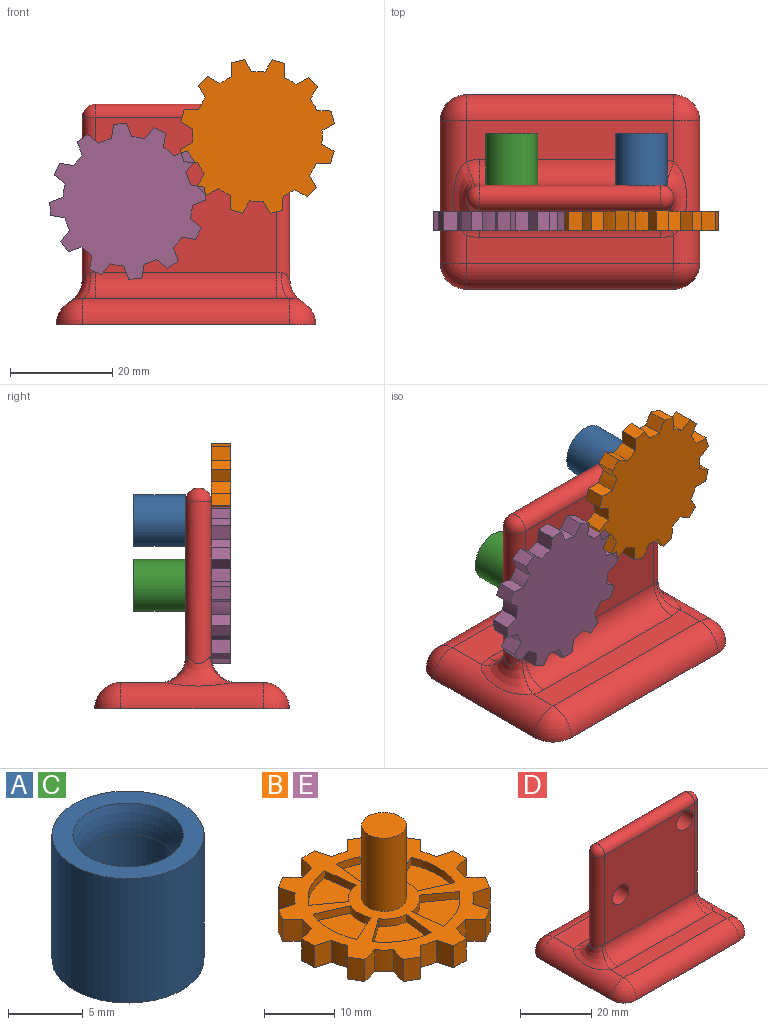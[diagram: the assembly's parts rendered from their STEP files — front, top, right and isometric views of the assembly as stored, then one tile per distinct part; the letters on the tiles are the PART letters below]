
ASSEMBLY  parts=5 mates=4
PART A: 6 faces, bbox 10.2x10.2x11.6 mm
  f0: cylinder r=3.17mm len=6.35mm, axis (0,0,-1), area 107.8mm2, adj f3,f4
  f1: cylinder r=5.08mm len=10.16mm, axis (0,0,-1), area 324.3mm2, adj f2,f5
  f2: plane 10.16x10.16mm, normal (0,0,1), area 38.5mm2, adj f1,f3
  f3: torus R=8.26mm, axis (0,0,1), area 48.2mm2, adj f0,f2
  f4: plane 6.35x6.35mm, normal (0,0,1), area 31.7mm2, adj f0
  f5: plane 10.16x10.16mm, normal (0,0,-1), area 81.1mm2, adj f1
PART B: 82 faces, bbox 30.5x30.5x16.5 mm
  f0: plane 30.48x30.48mm, normal (0,0,1), area 347.6mm2, adj f1,f2,f3,f4,f5,f6,f7,f8
  f1: plane 3.81x2.7mm, normal (-0.26,0.97,0), area 10.6mm2, adj f0,f2,f48,f49
  f2: cylinder r=12.7mm len=3.81mm, axis (0,0,-1), area 10.1mm2, adj f0,f1,f3,f49
  f3: plane 3.81x2.7mm, normal (0.97,-0.26,0), area 10.6mm2, adj f0,f2,f4,f49
  f4: plane 3.81x2.2mm, normal (0.5,0.87,0), area 9.7mm2, adj f0,f3,f5,f49
  f5: plane 3.81x1.97mm, normal (-0.71,0.71,0), area 10.6mm2, adj f0,f4,f6,f49
  f6: cylinder r=12.7mm len=3.81mm, axis (0,0,-1), area 10.1mm2, adj f0,f5,f7,f49
  f7: plane 3.81x2.7mm, normal (0.97,0.26,0), area 10.6mm2, adj f0,f6,f8,f49
  f8: plane 3.81x2.54mm, normal (0,1,0), area 9.7mm2, adj f0,f7,f9,f49
  f9: plane 3.81x2.7mm, normal (-0.97,0.26,0), area 10.6mm2, adj f0,f8,f10,f49
  f10: cylinder r=12.7mm len=3.81mm, axis (0,0,-1), area 10.1mm2, adj f0,f9,f11,f49
  f11: plane 3.81x1.97mm, normal (0.71,0.71,0), area 10.6mm2, adj f0,f10,f12,f49
  f12: plane 3.81x2.2mm, normal (-0.5,0.87,0), area 9.7mm2, adj f0,f11,f13,f49
  f13: plane 3.81x2.7mm, normal (-0.97,-0.26,0), area 10.6mm2, adj f0,f12,f14,f49
  f14: cylinder r=12.7mm len=3.81mm, axis (0,0,-1), area 10.1mm2, adj f0,f13,f15,f49
  f15: plane 3.81x2.7mm, normal (0.26,0.97,0), area 10.6mm2, adj f0,f14,f16,f49
  f16: plane 3.81x2.2mm, normal (-0.87,0.5,0), area 9.7mm2, adj f0,f15,f17,f49
  f17: plane 3.81x1.97mm, normal (-0.71,-0.71,0), area 10.6mm2, adj f0,f16,f18,f49
  f18: cylinder r=12.7mm len=3.81mm, axis (0,0,-1), area 10.1mm2, adj f0,f17,f19,f49
  f19: plane 3.81x2.7mm, normal (-0.26,0.97,0), area 10.6mm2, adj f0,f18,f20,f49
  f20: plane 3.81x2.54mm, normal (-1,0,0), area 9.7mm2, adj f0,f19,f21,f49
  f21: plane 3.81x2.7mm, normal (-0.26,-0.97,0), area 10.6mm2, adj f0,f20,f22,f49
  f22: cylinder r=12.7mm len=3.81mm, axis (0,0,-1), area 10.1mm2, adj f0,f21,f23,f49
  f23: plane 3.81x1.97mm, normal (-0.71,0.71,0), area 10.6mm2, adj f0,f22,f24,f49
  f24: plane 3.81x2.2mm, normal (-0.87,-0.5,0), area 9.7mm2, adj f0,f23,f25,f49
  f25: plane 3.81x2.7mm, normal (0.26,-0.97,0), area 10.6mm2, adj f0,f24,f26,f49
  f26: cylinder r=12.7mm len=3.81mm, axis (0,0,-1), area 10.1mm2, adj f0,f25,f27,f49
  f27: plane 3.81x2.7mm, normal (-0.97,0.26,0), area 10.6mm2, adj f0,f26,f28,f49
  f28: plane 3.81x2.2mm, normal (-0.5,-0.87,0), area 9.7mm2, adj f0,f27,f29,f49
  f29: plane 3.81x1.97mm, normal (0.71,-0.71,0), area 10.6mm2, adj f0,f28,f30,f49
  f30: cylinder r=12.7mm len=3.81mm, axis (0,0,-1), area 10.1mm2, adj f0,f29,f31,f49
  f31: plane 3.81x2.7mm, normal (-0.97,-0.26,0), area 10.6mm2, adj f0,f30,f32,f49
  f32: plane 3.81x2.54mm, normal (0,-1,0), area 9.7mm2, adj f0,f31,f33,f49
  f33: plane 3.81x2.7mm, normal (0.97,-0.26,0), area 10.6mm2, adj f0,f32,f34,f49
  f34: cylinder r=12.7mm len=3.81mm, axis (0,0,-1), area 10.1mm2, adj f0,f33,f35,f49
  f35: plane 3.81x1.97mm, normal (-0.71,-0.71,0), area 10.6mm2, adj f0,f34,f36,f49
  f36: plane 3.81x2.2mm, normal (0.5,-0.87,0), area 9.7mm2, adj f0,f35,f37,f49
  f37: plane 3.81x2.7mm, normal (0.97,0.26,0), area 10.6mm2, adj f0,f36,f38,f49
  f38: cylinder r=12.7mm len=3.81mm, axis (0,0,-1), area 10.1mm2, adj f0,f37,f39,f49
  f39: plane 3.81x2.7mm, normal (-0.26,-0.97,0), area 10.6mm2, adj f0,f38,f40,f49
  f40: plane 3.81x2.2mm, normal (0.87,-0.5,0), area 9.7mm2, adj f0,f39,f41,f49
  f41: plane 3.81x1.97mm, normal (0.71,0.71,0), area 10.6mm2, adj f0,f40,f42,f49
  f42: cylinder r=12.7mm len=3.81mm, axis (0,0,-1), area 10.1mm2, adj f0,f41,f43,f49
  f43: plane 3.81x2.7mm, normal (0.26,-0.97,0), area 10.6mm2, adj f0,f42,f44,f49
  f44: plane 3.81x2.54mm, normal (1,0,0), area 9.7mm2, adj f0,f43,f45,f49
  f45: plane 3.81x2.7mm, normal (0.26,0.97,0), area 10.6mm2, adj f0,f44,f46,f49
  f46: cylinder r=12.7mm len=3.81mm, axis (0,0,-1), area 10.1mm2, adj f0,f45,f47,f49
  f47: plane 3.81x1.97mm, normal (0.71,-0.71,0), area 10.6mm2, adj f0,f46,f48,f49
  f48: plane 3.81x2.2mm, normal (0.87,0.5,0), area 9.7mm2, adj f0,f1,f47,f49
  f49: plane 30.48x30.48mm, normal (0,0,-1), area 607.3mm2, adj f1,f2,f3,f4,f5,f6,f7,f8
  f50: plane 4.62x3.36mm, normal (-0.59,0.81,0), area 7.3mm2, adj f0,f51,f53,f54
  f51: cylinder r=10.79mm len=7.61mm, axis (0,0,1), area 11.5mm2, adj f0,f50,f52,f54
  f52: plane 5.68x1.27mm, normal (0.99,-0.1,0), area 7.3mm2, adj f0,f51,f53,f54
  f53: cylinder r=5.08mm len=3.58mm, axis (0,0,1), area 5.4mm2, adj f0,f50,f52,f54
  f54: plane 8.2x7.75mm, normal (0,0,1), area 38mm2, adj f50,f51,f52,f53
  f55: plane 5.68x1.27mm, normal (0.99,0.1,0), area 7.3mm2, adj f0,f56,f58,f59
  f56: cylinder r=10.79mm len=7.61mm, axis (0,0,1), area 11.5mm2, adj f0,f55,f57,f59
  f57: plane 4.62x3.36mm, normal (-0.59,-0.81,0), area 7.3mm2, adj f0,f56,f58,f59
  f58: cylinder r=5.08mm len=3.58mm, axis (0,0,1), area 5.4mm2, adj f0,f55,f57,f59
  f59: plane 8.2x7.75mm, normal (0,0,1), area 38mm2, adj f55,f56,f57,f58
  f60: cylinder r=5.08mm len=3.58mm, axis (0,0,1), area 5.4mm2, adj f0,f61,f63,f64
  f61: plane 5.68x1.27mm, normal (-0.99,-0.1,0), area 7.3mm2, adj f0,f60,f62,f64
  f62: cylinder r=10.79mm len=7.61mm, axis (0,0,1), area 11.5mm2, adj f0,f61,f63,f64
  f63: plane 4.62x3.36mm, normal (0.59,0.81,0), area 7.3mm2, adj f0,f60,f62,f64
  f64: plane 8.2x7.75mm, normal (0,0,1), area 38mm2, adj f60,f61,f62,f63
  f65: cylinder r=10.79mm len=8.78mm, axis (0,0,1), area 11.5mm2, adj f0,f66,f68,f69
  f66: plane 5.22x2.32mm, normal (0.41,-0.91,0), area 7.3mm2, adj f0,f65,f67,f69
  f67: cylinder r=5.08mm len=4.13mm, axis (0,0,1), area 5.4mm2, adj f0,f66,f68,f69
  f68: plane 5.22x2.32mm, normal (0.41,0.91,0), area 7.3mm2, adj f0,f65,f67,f69
  f69: plane 8.78x6.15mm, normal (0,0,1), area 38mm2, adj f65,f66,f67,f68
  f70: plane 4.62x3.36mm, normal (0.59,-0.81,0), area 7.3mm2, adj f0,f71,f73,f74
  f71: cylinder r=10.79mm len=7.61mm, axis (0,0,1), area 11.5mm2, adj f0,f70,f72,f74
  f72: plane 5.68x1.27mm, normal (-0.99,0.1,0), area 7.3mm2, adj f0,f71,f73,f74
  f73: cylinder r=5.08mm len=3.58mm, axis (0,0,1), area 5.4mm2, adj f0,f70,f72,f74
  f74: plane 8.2x7.75mm, normal (0,0,1), area 38mm2, adj f70,f71,f72,f73
  f75: plane 5.22x2.32mm, normal (-0.41,-0.91,0), area 7.3mm2, adj f0,f76,f78,f79
  f76: cylinder r=10.79mm len=8.78mm, axis (0,0,1), area 11.5mm2, adj f0,f75,f77,f79
  f77: plane 5.22x2.32mm, normal (-0.41,0.91,0), area 7.3mm2, adj f0,f76,f78,f79
  f78: cylinder r=5.08mm len=4.13mm, axis (0,0,1), area 5.4mm2, adj f0,f75,f77,f79
  f79: plane 8.78x6.15mm, normal (0,0,1), area 38mm2, adj f75,f76,f77,f78
  f80: cylinder r=3.17mm len=12.7mm, axis (0,0,-1), area 253.4mm2, adj f0,f81
  f81: plane 6.35x6.35mm, normal (0,0,1), area 31.7mm2, adj f80
PART C: same geometry as A
PART D: 28 faces, bbox 50.8x38.1x43.2 mm
  f0: plane 40.64x5.52mm, normal (0,0,1), area 207.2mm2, adj f5,f8,f9,f20,f21,f22
  f1: plane 40.64x8.06mm, normal (0,0,1), area 310.4mm2, adj f4,f5,f8,f25,f26,f27
  f2: plane 50.8x38.1mm, normal (0,0,-1), area 1913.3mm2, adj f3,f4,f5,f6,f7,f8,f9,f10
  f3: sphere r=5.08mm, area 40.5mm2, adj f2,f4,f5
  f4: cylinder r=5.08mm len=40.64mm, axis (1,0,0), area 324.3mm2, adj f1,f2,f3,f6
  f5: cylinder r=5.08mm len=27.94mm, axis (0,-1,0), area 195.4mm2, adj f0,f1,f2,f3,f7,f23
  f6: sphere r=5.08mm, area 40.5mm2, adj f2,f4,f8
  f7: sphere r=5.08mm, area 40.5mm2, adj f2,f5,f9
  f8: cylinder r=5.08mm len=27.94mm, axis (0,1,0), area 195.4mm2, adj f0,f1,f2,f6,f10,f24
  f9: cylinder r=5.08mm len=40.64mm, axis (-1,0,0), area 324.3mm2, adj f0,f2,f7,f10
  f10: sphere r=5.08mm, area 40.5mm2, adj f2,f8,f9
  f11: plane 35.56x30.48mm, normal (0,1,0), area 1018mm2, adj f13,f14,f15,f17,f19,f27
  f12: plane 35.56x30.48mm, normal (0,-1,0), area 1018mm2, adj f13,f14,f15,f17,f19,f20
  f13: cylinder r=3.24mm len=6.48mm, axis (0,1,0), area 103.4mm2, adj f11,f12
  f14: cylinder r=3.24mm len=6.48mm, axis (0,1,0), area 103.4mm2, adj f11,f12
  f15: cylinder r=2.54mm len=31.84mm, axis (0,0,1), area 247.5mm2, adj f11,f12,f16,f22,f24,f26
  f16: sphere r=2.54mm, area 20.3mm2, adj f15,f17
  f17: cylinder r=2.54mm len=35.56mm, axis (-1,0,0), area 283.8mm2, adj f11,f12,f16,f18
  f18: sphere r=2.54mm, area 20.3mm2, adj f17,f19
  f19: cylinder r=2.54mm len=31.84mm, axis (0,0,1), area 247.5mm2, adj f11,f12,f18,f21,f23,f25
  f20: cylinder r=5.08mm len=35.56mm, axis (1,0,0), area 283.8mm2, adj f0,f12,f21,f22
  f21: torus R=7.62mm, axis (0,0,1), area 11.9mm2, adj f0,f19,f20,f23
  f22: torus R=7.62mm, axis (0,0,1), area 11.9mm2, adj f0,f15,f20,f24
  f23: bspline ~15.08x5.76mm, area 60.3mm2, adj f5,f19,f21,f25
  f24: bspline ~15.08x5.76mm, area 60.3mm2, adj f8,f15,f22,f26
  f25: torus R=7.62mm, axis (0,0,1), area 11.9mm2, adj f1,f19,f23,f27
  f26: torus R=7.62mm, axis (0,0,1), area 11.9mm2, adj f1,f15,f24,f27
  f27: cylinder r=5.08mm len=35.56mm, axis (-1,0,0), area 283.8mm2, adj f1,f11,f25,f26
PART E: same geometry as B
PLACE A rot(axis=(0.1,-0.7,0.7),168.9deg) t=(13.97,8.89,36.83)mm
PLACE B rot(axis=(-0.98,0.14,0.14),91.1deg) t=(13.97,-7.62,36.83)mm
PLACE C rot(axis=(0.54,-0.6,0.6),123.3deg) t=(-11.43,8.89,24.13)mm
PLACE D rot(axis=(0,-1,-0.02),0deg) t=(-25.4,-19.05,0)mm
PLACE E rot(axis=(-0.61,0.56,0.56),116.8deg) t=(-11.43,-7.62,24.13)mm
MATE revolute E.f2 <-> D.f14  axis (0,-1,0) through (-11.43,-3.81,24.13)mm
MATE fastened C.f0 <-> E.f2  axis (0,1,0) through (-11.43,8.89,24.13)mm
MATE revolute B.f2 <-> D.f13  axis (0,-1,0) through (13.97,-3.81,36.83)mm
MATE fastened A.f0 <-> B.f2  axis (0,1,0) through (13.97,8.89,36.83)mm
